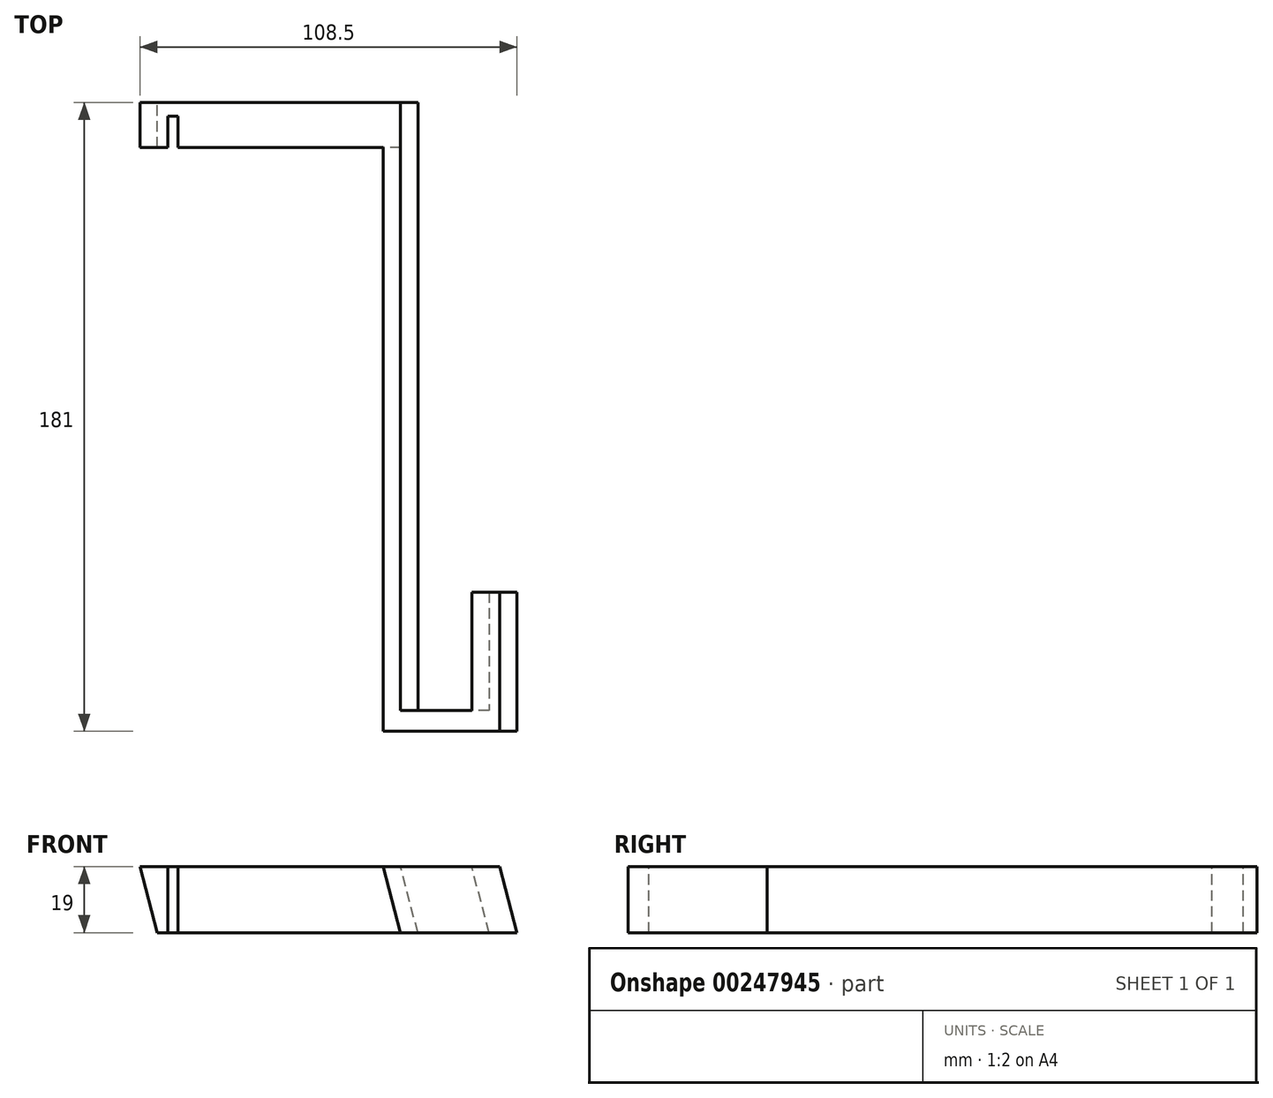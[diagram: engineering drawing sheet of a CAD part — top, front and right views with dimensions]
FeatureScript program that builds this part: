
annotation { "Feature Type Name" : "Feature", "Feature Type Description" : "" }
export const myFeature = defineFeature(function(context is Context, id is Id, definition is map)
    precondition{}
    {
        {
            var Q0;
            Q0=qCreatedBy(makeId("Top.planeOp"),FACE);
            var sketch = newSketch(context, id + "F0", { "sketchPlane" : qUnion([Q0])});
            skLineSegment(sketch, "E0", {"start": v(-56.64, 50.5) * mm, "end": v(-66.64, 50.5) * mm});
            skLineSegment(sketch, "E1", {"start": v(-66.64, 50.5) * mm, "end": v(-66.64, 63.5) * mm});
            skLineSegment(sketch, "E2", {"start": v(-66.64, 63.5) * mm, "end": v(8.36, 63.5) * mm});
            skLineSegment(sketch, "E3", {"start": v(8.36, 63.5) * mm, "end": v(8.36, -111.5) * mm});
            skLineSegment(sketch, "E4", {"start": v(3.36, 50.5) * mm, "end": v(3.36, -117.5) * mm});
            skLineSegment(sketch, "E5", {"start": v(3.36, -117.5) * mm, "end": v(36.86, -117.5) * mm});
            skLineSegment(sketch, "E6", {"start": v(36.86, -117.5) * mm, "end": v(36.86, -77.5) * mm});
            skLineSegment(sketch, "E7", {"start": v(36.86, -77.5) * mm, "end": v(28.86, -77.5) * mm});
            skLineSegment(sketch, "E8", {"start": v(28.86, -77.5) * mm, "end": v(28.86, -111.5) * mm});
            skLineSegment(sketch, "E9", {"start": v(28.86, -111.5) * mm, "end": v(8.36, -111.5) * mm});
            skLineSegment(sketch, "E10.top", {"start": v(3.36, 50.5) * mm, "end": v(-56.64, 50.5) * mm});
            skPoint(sketch, "E11.start.orphan", {"position": v(-60.64, 59.5) * mm});
            skPoint(sketch, "E12.orphan", {"position": v(-60.64, 50.5) * mm});
            skSolve(sketch);
        }
        {
            var Q0;
            Q0=qCreatedBy(makeId("Top.planeOp"),FACE);
            cPlane(context, id + "F1", {"entities" : qUnion([Q0]), "cplaneType" : CPlaneType.OFFSET, "offset" : 19 * mm, "width" : 150 * mm, "height" : 150 * mm});
        }
        {
            var Q0;
            Q0=qCreatedBy(id+"F1.planeOp",FACE);
            var sketch = newSketch(context, id + "F2", { "sketchPlane" : qUnion([Q0])});
            skLineSegment(sketch, "E13", {"start": v(-61.64, 50.5) * mm, "end": v(-71.64, 50.5) * mm});
            skLineSegment(sketch, "E14", {"start": v(-71.64, 50.5) * mm, "end": v(-71.64, 63.5) * mm});
            skLineSegment(sketch, "E15", {"start": v(-71.64, 63.5) * mm, "end": v(3.36, 63.5) * mm});
            skLineSegment(sketch, "E16", {"start": v(3.36, 63.5) * mm, "end": v(3.36, -111.5) * mm});
            skLineSegment(sketch, "E17", {"start": v(-1.64, 50.5) * mm, "end": v(-1.64, -117.5) * mm});
            skLineSegment(sketch, "E18", {"start": v(-1.64, -117.5) * mm, "end": v(31.86, -117.5) * mm});
            skLineSegment(sketch, "E19", {"start": v(31.86, -117.5) * mm, "end": v(31.86, -77.5) * mm});
            skLineSegment(sketch, "E20", {"start": v(31.86, -77.5) * mm, "end": v(23.86, -77.5) * mm});
            skLineSegment(sketch, "E21", {"start": v(23.86, -77.5) * mm, "end": v(23.86, -111.5) * mm});
            skLineSegment(sketch, "E22", {"start": v(23.86, -111.5) * mm, "end": v(3.36, -111.5) * mm});
            skLineSegment(sketch, "E23.top", {"start": v(-1.64, 50.5) * mm, "end": v(-61.64, 50.5) * mm});
            skPoint(sketch, "E24.start.orphan", {"position": v(-65.64, 59.5) * mm});
            skPoint(sketch, "E25.orphan", {"position": v(-65.64, 50.5) * mm});
            skSolve(sketch);
        }
        {
            var Q0;
            Q0=makeQuery(id+"F0.imprint","IMPRINT",FACE,{"disambiguationData":[TD([[makeQuery(id+"F0.imprint","IMPRINT",EDGE,{"derivedFrom":sQuery(id+"F0.wireOp",EDGE,"E0")}),-1.0]])]});
            var Q1;
            Q1=makeQuery(id+"F2.imprint","IMPRINT",FACE,{"disambiguationData":[TD([[makeQuery(id+"F2.imprint","IMPRINT",EDGE,{"derivedFrom":sQuery(id+"F2.wireOp",EDGE,"E13")}),-1.0]])]});
            loft(context, id + "F3", {"sheetProfilesArray" : [{ "sheetProfileEntities" : qUnion([Q0]) }, { "sheetProfileEntities" : qUnion([Q1]) }]});
        }
        {
            var Q0;
            Q0=makeQuery(id+"F3.opLoft","CAP_FACE",FACE,{"disambiguationData":[OSD([makeQuery(id+"F2.imprint","IMPRINT",FACE,{"disambiguationData":[TD([[makeQuery(id+"F2.imprint","IMPRINT",EDGE,{"derivedFrom":sQuery(id+"F2.wireOp",EDGE,"E13")}),-1.0]])]})])],"isStart":true});
            var sketch = newSketch(context, id + "F4", { "sketchPlane" : qUnion([Q0])});
            skLineSegment(sketch, "E26.bottom", {"start": v(-60.64, 50.5) * mm, "end": v(-63.64, 50.5) * mm});
            skLineSegment(sketch, "E26.top", {"start": v(-60.64, 59.5) * mm, "end": v(-63.64, 59.5) * mm});
            skLineSegment(sketch, "E26.left", {"start": v(-60.64, 50.5) * mm, "end": v(-60.64, 59.5) * mm});
            skLineSegment(sketch, "E26.right", {"start": v(-63.64, 50.5) * mm, "end": v(-63.64, 59.5) * mm});
            skSolve(sketch);
        }
        {
            var Q0;
            Q0=makeQuery(id+"F4.imprint","IMPRINT",FACE,{"disambiguationData":[TD([[makeQuery(id+"F4.imprint","IMPRINT",EDGE,{"derivedFrom":sQuery(id+"F4.wireOp",EDGE,"E26.bottom")}),1.0]])]});
            extrude(context, id + "F5", {"entities" : qUnion([Q0]), "operationType" : NewBodyOperationType.REMOVE, "oppositeDirection" : true, "depth" : 25 * mm});
        }
    });
